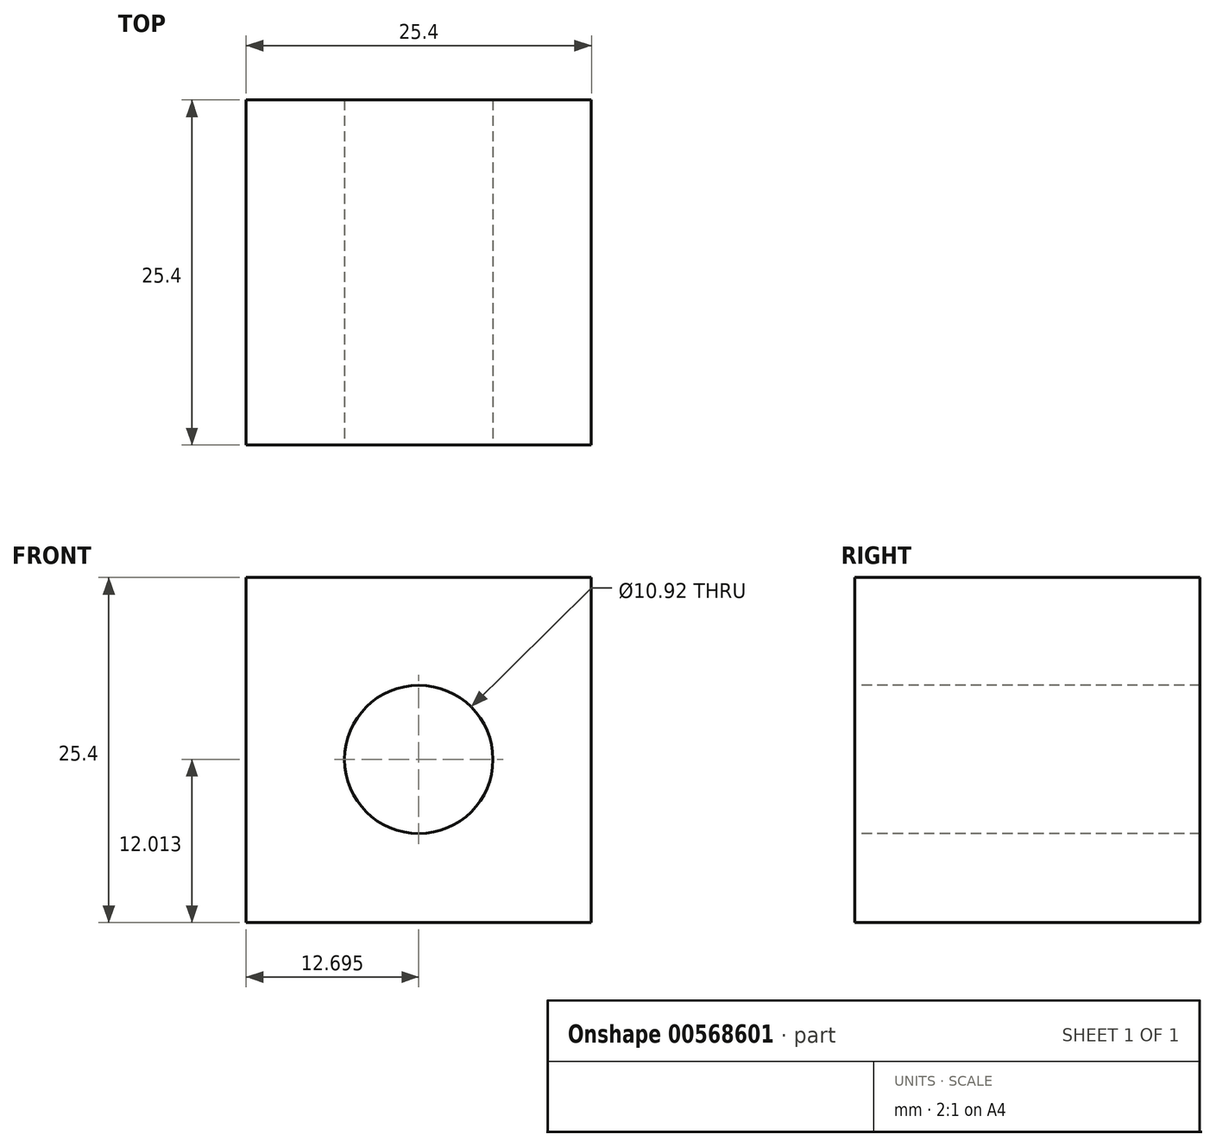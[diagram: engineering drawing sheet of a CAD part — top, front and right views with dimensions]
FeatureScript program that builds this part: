
annotation { "Feature Type Name" : "Feature", "Feature Type Description" : "" }
export const myFeature = defineFeature(function(context is Context, id is Id, definition is map)
    precondition{}
    {
        {
            var Q0;
            Q0=qCreatedBy(makeId("Front.planeOp"),FACE);
            var sketch = newSketch(context, id + "F0", { "sketchPlane" : qUnion([Q0])});
            skLineSegment(sketch, "E0.bottom", {"start": v(-28.72, 31.33) * mm, "end": v(-3.32, 31.33) * mm});
            skLineSegment(sketch, "E0.top", {"start": v(-28.72, 5.93) * mm, "end": v(-3.32, 5.93) * mm});
            skLineSegment(sketch, "E0.left", {"start": v(-28.72, 31.33) * mm, "end": v(-28.72, 5.93) * mm});
            skLineSegment(sketch, "E0.right", {"start": v(-3.32, 31.33) * mm, "end": v(-3.32, 5.93) * mm});
            skSolve(sketch);
        }
        {
            var Q0;
            Q0 = qSketchRegion(id + "F0", true);
            extrude(context, id + "F1", {"entities" : qUnion([Q0]), "depth" : 25.4 * mm, "offsetDistance" : 25.4 * mm});
        }
        {
            var Q0;
            Q0=makeQuery(id+"F1.opExtrude","CAP_FACE",FACE,{"disambiguationData":[OSD([sQuery(id+"F0.wireOp",EDGE,"E0.bottom"),sQuery(id+"F0.wireOp",EDGE,"E0.top"),sQuery(id+"F0.wireOp",EDGE,"E0.left"),sQuery(id+"F0.wireOp",EDGE,"E0.right")])],"isStart":false});
            var sketch = newSketch(context, id + "F2", { "sketchPlane" : qUnion([Q0])});
            skCircle(sketch, "E1", {"center": v(-16.02, 17.94) * mm, "radius": 5.46 * mm});
            skSolve(sketch);
        }
        {
            var Q0;
            Q0=makeQuery(id+"F2.imprint","IMPRINT",FACE,{"disambiguationData":[TD([[makeQuery(id+"F2.imprint","IMPRINT",EDGE,{"derivedFrom":sQuery(id+"F2.wireOp",EDGE,"E1")}),1.0]])]});
            extrude(context, id + "F3", {"entities" : qUnion([Q0]), "operationType" : NewBodyOperationType.REMOVE, "endBound" : BoundingType.THROUGH_ALL, "oppositeDirection" : true, "depth" : 25.4 * mm, "offsetDistance" : 25.4 * mm});
        }
    });
